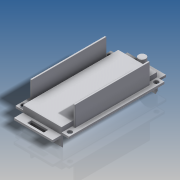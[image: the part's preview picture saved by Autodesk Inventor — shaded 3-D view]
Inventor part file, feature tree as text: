
AUTODESK INVENTOR PART (.ipt)
format: ipt  version: 2016 SP2 (Build 200236200, 236)  size: 374,784 bytes
history: native  units: in
note: dims shown in document units (in); Inventor stores cm internally (conversion verified against a paired STEP export)
features: extrude x10, sketch x4, chamfer x1, fillet x1, projected_geometry x1
ambient origin geometry x8: Origin, YZ Plane, XZ Plane, XY Plane, X Axis, Y Axis, Z Axis, Center Point
bodies: Solid1 (feature_tree)
feature tree (17):
  sketch  "Sketch2"  dims[d0=1.1339in d1=2.0157in]
  extrude  "Extrusion1"  Depth=2.0157in
  extrude  "Extrusion2"  Depth=0.8819in
  extrude  "Extrusion3"  Depth=1.5748in
  extrude  "Extrusion4"  Depth=0.0039in
  sketch  "Sketch4"  dims[d4=0.0315in d5=1.5748in]
  extrude  "Extrusion5"  Depth=0.9764in
  extrude  "Extrusion6"  Depth=0.0472in TaperAngle=0.0deg
  extrude  "Extrusion7"  Depth=0.0945in TaperAngle=0.0deg
  extrude  "Extrusion8"  Depth=0.4252in TaperAngle=0.0deg
  extrude  "Extrusion9"  Depth=0.0472in
  extrude  "Extrusion10"  Depth=0.189in
  chamfer  "Chamfer1"  Distance=0.1732in
  fillet  "Fillet1"  Radius=0.1575in
  sketch  "Sketch3"  dims[d2=0.8189in d3=0.8819in]
  projected_geometry  "Projected Loop1"
  sketch  "Sketch5"  dims[d6=0.0945in d7=1.8268in d8=0.9764in d9=0.0472in d10=0.0in d11=0.0945in d12=0.0in d13=0.4252in d14=0.0in d15=0.0472in d16=0.189in d17=0.1732in d18=0.1575in d19=0.0472in d20=0.2047in d21=0.0157in d22=0.4252in d23=0.0in d24=0.0945in d25=0.3465in d26=0.0315in d27=0.1575in d28=0.0945in d29=0.0315in d30=0.1575in d31=0.0945in d32=0.0945in d33=0.4252in d34=0.0in d35=0.4252in d36=0.0in d37=0.0315in d38=0.0in d39=0.2205in d40=0.0in d41=0.1732in d42=0.0in d43=0.4252in d44=0.0315in d45=0.1109in d46=0.2074in d47=0.1732in d48=0.0in d49=0.0236in d50=0.0315in d51=45.0deg d52=0.0039in]
